FCSTD DOCUMENT  (FreeCAD 0.20R)
Label: even_better_inner_plate
License: All rights reserved
LicenseURL: http://en.wikipedia.org/wiki/All_rights_reserved
objects: Sketcher::SketchObject×1
note: 1 computed .brp shape members not serialized (recipe doc carries the construction recipe); baked Part::Feature solids carry a one-line shape summary decoded from their .brp

FEATURE [Sketcher::SketchObject] Sketch
  FullyConstrained = true
  sketch-geometry (934):
    g0: LineSegment StartX=3.025 StartY=-7.2875 StartZ=0 EndX=16.025 EndY=-7.2875 EndZ=0
    g1: LineSegment StartX=3.025 StartY=-21.2875 StartZ=0 EndX=16.025 EndY=-21.2875 EndZ=0
    g2: LineSegment StartX=2.525 StartY=-7.7875 StartZ=0 EndX=2.525 EndY=-20.7875 EndZ=0
    g3: LineSegment StartX=16.525 StartY=-7.7875 StartZ=0 EndX=16.525 EndY=-20.7875 EndZ=0
    g4: ArcOfCircle CenterX=3.025 CenterY=-7.7875 CenterZ=0 NormalX=0 NormalY=0 NormalZ=1 AngleXU=0 Radius=0.5 StartAngle=1.5708 EndAngle=3.14159
    g5: ArcOfCircle CenterX=16.025 CenterY=-7.7875 CenterZ=0 NormalX=0 NormalY=0 NormalZ=1 AngleXU=0 Radius=0.5 StartAngle=0 EndAngle=1.5708
    g6: ArcOfCircle CenterX=3.025 CenterY=-20.7875 CenterZ=0 NormalX=0 NormalY=0 NormalZ=1 AngleXU=0 Radius=0.5 StartAngle=3.14159 EndAngle=4.71239
    g7: ArcOfCircle CenterX=16.025 CenterY=-20.7875 CenterZ=0 NormalX=0 NormalY=0 NormalZ=1 AngleXU=0 Radius=0.5 StartAngle=4.71239 EndAngle=6.28319
    g8: LineSegment StartX=41.125 StartY=-7.2875 StartZ=0 EndX=54.125 EndY=-7.2875 EndZ=0
    g9: LineSegment StartX=41.125 StartY=-21.2875 StartZ=0 EndX=54.125 EndY=-21.2875 EndZ=0
    g10: LineSegment StartX=40.625 StartY=-7.7875 StartZ=0 EndX=40.625 EndY=-20.7875 EndZ=0
    g11: LineSegment StartX=54.625 StartY=-7.7875 StartZ=0 EndX=54.625 EndY=-20.7875 EndZ=0
    g12: ArcOfCircle CenterX=41.125 CenterY=-7.7875 CenterZ=0 NormalX=0 NormalY=0 NormalZ=1 AngleXU=0 Radius=0.5 StartAngle=1.5708 EndAngle=3.14159
    g13: ArcOfCircle CenterX=54.125 CenterY=-7.7875 CenterZ=0 NormalX=0 NormalY=0 NormalZ=1 AngleXU=0 Radius=0.5 StartAngle=0 EndAngle=1.5708
    g14: ArcOfCircle CenterX=41.125 CenterY=-20.7875 CenterZ=0 NormalX=0 NormalY=0 NormalZ=1 AngleXU=0 Radius=0.5 StartAngle=3.14159 EndAngle=4.71239
    g15: ArcOfCircle CenterX=54.125 CenterY=-20.7875 CenterZ=0 NormalX=0 NormalY=0 NormalZ=1 AngleXU=0 Radius=0.5 StartAngle=4.71239 EndAngle=6.28319
    g16: LineSegment StartX=60.175 StartY=-7.2875 StartZ=0 EndX=73.175 EndY=-7.2875 EndZ=0
    g17: LineSegment StartX=60.175 StartY=-21.2875 StartZ=0 EndX=73.175 EndY=-21.2875 EndZ=0
    g18: LineSegment StartX=59.675 StartY=-7.7875 StartZ=0 EndX=59.675 EndY=-20.7875 EndZ=0
    g19: LineSegment StartX=73.675 StartY=-7.7875 StartZ=0 EndX=73.675 EndY=-20.7875 EndZ=0
    g20: ArcOfCircle CenterX=60.175 CenterY=-7.7875 CenterZ=0 NormalX=0 NormalY=0 NormalZ=1 AngleXU=0 Radius=0.5 StartAngle=1.5708 EndAngle=3.14159
    g21: ArcOfCircle CenterX=73.175 CenterY=-7.7875 CenterZ=0 NormalX=0 NormalY=0 NormalZ=1 AngleXU=0 Radius=0.5 StartAngle=0 EndAngle=1.5708
    g22: ArcOfCircle CenterX=60.175 CenterY=-20.7875 CenterZ=0 NormalX=0 NormalY=0 NormalZ=1 AngleXU=0 Radius=0.5 StartAngle=3.14159 EndAngle=4.71239
    g23: ArcOfCircle CenterX=73.175 CenterY=-20.7875 CenterZ=0 NormalX=0 NormalY=0 NormalZ=1 AngleXU=0 Radius=0.5 StartAngle=4.71239 EndAngle=6.28319
    g24: LineSegment StartX=79.225 StartY=-7.2875 StartZ=0 EndX=92.225 EndY=-7.2875 EndZ=0
    g25: LineSegment StartX=79.225 StartY=-21.2875 StartZ=0 EndX=92.225 EndY=-21.2875 EndZ=0
    g26: LineSegment StartX=78.725 StartY=-7.7875 StartZ=0 EndX=78.725 EndY=-20.7875 EndZ=0
    g27: LineSegment StartX=92.725 StartY=-7.7875 StartZ=0 EndX=92.725 EndY=-20.7875 EndZ=0
    g28: ArcOfCircle CenterX=79.225 CenterY=-7.7875 CenterZ=0 NormalX=0 NormalY=0 NormalZ=1 AngleXU=0 Radius=0.5 StartAngle=1.5708 EndAngle=3.14159
    g29: ArcOfCircle CenterX=92.225 CenterY=-7.7875 CenterZ=0 NormalX=0 NormalY=0 NormalZ=1 AngleXU=0 Radius=0.5 StartAngle=0 EndAngle=1.5708
    g30: ArcOfCircle CenterX=79.225 CenterY=-20.7875 CenterZ=0 NormalX=0 NormalY=0 NormalZ=1 AngleXU=0 Radius=0.5 StartAngle=3.14159 EndAngle=4.71239
    g31: ArcOfCircle CenterX=92.225 CenterY=-20.7875 CenterZ=0 NormalX=0 NormalY=0 NormalZ=1 AngleXU=0 Radius=0.5 StartAngle=4.71239 EndAngle=6.28319
    g32: LineSegment StartX=98.275 StartY=-7.2875 StartZ=0 EndX=111.275 EndY=-7.2875 EndZ=0
    g33: LineSegment StartX=98.275 StartY=-21.2875 StartZ=0 EndX=111.275 EndY=-21.2875 EndZ=0
    g34: LineSegment StartX=97.775 StartY=-7.7875 StartZ=0 EndX=97.775 EndY=-20.7875 EndZ=0
    g35: LineSegment StartX=111.775 StartY=-7.7875 StartZ=0 EndX=111.775 EndY=-20.7875 EndZ=0
    g36: ArcOfCircle CenterX=98.275 CenterY=-7.7875 CenterZ=0 NormalX=0 NormalY=0 NormalZ=1 AngleXU=0 Radius=0.5 StartAngle=1.5708 EndAngle=3.14159
    g37: ArcOfCircle CenterX=111.275 CenterY=-7.7875 CenterZ=0 NormalX=0 NormalY=0 NormalZ=1 AngleXU=0 Radius=0.5 StartAngle=0 EndAngle=1.5708
    g38: ArcOfCircle CenterX=98.275 CenterY=-20.7875 CenterZ=0 NormalX=0 NormalY=0 NormalZ=1 AngleXU=0 Radius=0.5 StartAngle=3.14159 EndAngle=4.71239
    g39: ArcOfCircle CenterX=111.275 CenterY=-20.7875 CenterZ=0 NormalX=0 NormalY=0 NormalZ=1 AngleXU=0 Radius=0.5 StartAngle=4.71239 EndAngle=6.28319
    g40: LineSegment StartX=126.85 StartY=-7.2875 StartZ=0 EndX=139.85 EndY=-7.2875 EndZ=0
    g41: LineSegment StartX=126.85 StartY=-21.2875 StartZ=0 EndX=139.85 EndY=-21.2875 EndZ=0
    g42: LineSegment StartX=126.35 StartY=-7.7875 StartZ=0 EndX=126.35 EndY=-20.7875 EndZ=0
    g43: LineSegment StartX=140.35 StartY=-7.7875 StartZ=0 EndX=140.35 EndY=-20.7875 EndZ=0
    g44: ArcOfCircle CenterX=126.85 CenterY=-7.7875 CenterZ=0 NormalX=0 NormalY=0 NormalZ=1 AngleXU=0 Radius=0.5 StartAngle=1.5708 EndAngle=3.14159
    g45: ArcOfCircle CenterX=139.85 CenterY=-7.7875 CenterZ=0 NormalX=0 NormalY=0 NormalZ=1 AngleXU=0 Radius=0.5 StartAngle=0 EndAngle=1.5708
    g46: ArcOfCircle CenterX=126.85 CenterY=-20.7875 CenterZ=0 NormalX=0 NormalY=0 NormalZ=1 AngleXU=0 Radius=0.5 StartAngle=3.14159 EndAngle=4.71239
    g47: ArcOfCircle CenterX=139.85 CenterY=-20.7875 CenterZ=0 NormalX=0 NormalY=0 NormalZ=1 AngleXU=0 Radius=0.5 StartAngle=4.71239 EndAngle=6.28319
    g48: LineSegment StartX=145.9 StartY=-7.2875 StartZ=0 EndX=158.9 EndY=-7.2875 EndZ=0
    g49: LineSegment StartX=145.9 StartY=-21.2875 StartZ=0 EndX=158.9 EndY=-21.2875 EndZ=0
    g50: LineSegment StartX=145.4 StartY=-7.7875 StartZ=0 EndX=145.4 EndY=-20.7875 EndZ=0
    g51: LineSegment StartX=159.4 StartY=-7.7875 StartZ=0 EndX=159.4 EndY=-20.7875 EndZ=0
    g52: ArcOfCircle CenterX=145.9 CenterY=-7.7875 CenterZ=0 NormalX=0 NormalY=0 NormalZ=1 AngleXU=0 Radius=0.5 StartAngle=1.5708 EndAngle=3.14159
    g53: ArcOfCircle CenterX=158.9 CenterY=-7.7875 CenterZ=0 NormalX=0 NormalY=0 NormalZ=1 AngleXU=0 Radius=0.5 StartAngle=0 EndAngle=1.5708
    g54: ArcOfCircle CenterX=145.9 CenterY=-20.7875 CenterZ=0 NormalX=0 NormalY=0 NormalZ=1 AngleXU=0 Radius=0.5 StartAngle=3.14159 EndAngle=4.71239
    g55: ArcOfCircle CenterX=158.9 CenterY=-20.7875 CenterZ=0 NormalX=0 NormalY=0 NormalZ=1 AngleXU=0 Radius=0.5 StartAngle=4.71239 EndAngle=6.28319
    g56: LineSegment StartX=164.95 StartY=-7.2875 StartZ=0 EndX=177.95 EndY=-7.2875 EndZ=0
    g57: LineSegment StartX=164.95 StartY=-21.2875 StartZ=0 EndX=177.95 EndY=-21.2875 EndZ=0
    g58: LineSegment StartX=164.45 StartY=-7.7875 StartZ=0 EndX=164.45 EndY=-20.7875 EndZ=0
    g59: LineSegment StartX=178.45 StartY=-7.7875 StartZ=0 EndX=178.45 EndY=-20.7875 EndZ=0
    g60: ArcOfCircle CenterX=164.95 CenterY=-7.7875 CenterZ=0 NormalX=0 NormalY=0 NormalZ=1 AngleXU=0 Radius=0.5 StartAngle=1.5708 EndAngle=3.14159
    g61: ArcOfCircle CenterX=177.95 CenterY=-7.7875 CenterZ=0 NormalX=0 NormalY=0 NormalZ=1 AngleXU=0 Radius=0.5 StartAngle=0 EndAngle=1.5708
    g62: ArcOfCircle CenterX=164.95 CenterY=-20.7875 CenterZ=0 NormalX=0 NormalY=0 NormalZ=1 AngleXU=0 Radius=0.5 StartAngle=3.14159 EndAngle=4.71239
    g63: ArcOfCircle CenterX=177.95 CenterY=-20.7875 CenterZ=0 NormalX=0 NormalY=0 NormalZ=1 AngleXU=0 Radius=0.5 StartAngle=4.71239 EndAngle=6.28319
    g64: LineSegment StartX=184 StartY=-7.2875 StartZ=0 EndX=197 EndY=-7.2875 EndZ=0
    g65: LineSegment StartX=184 StartY=-21.2875 StartZ=0 EndX=197 EndY=-21.2875 EndZ=0
    g66: LineSegment StartX=183.5 StartY=-7.7875 StartZ=0 EndX=183.5 EndY=-20.7875 EndZ=0
    g67: LineSegment StartX=197.5 StartY=-7.7875 StartZ=0 EndX=197.5 EndY=-20.7875 EndZ=0
    g68: ArcOfCircle CenterX=184 CenterY=-7.7875 CenterZ=0 NormalX=0 NormalY=0 NormalZ=1 AngleXU=0 Radius=0.5 StartAngle=1.5708 EndAngle=3.14159
    g69: ArcOfCircle CenterX=197 CenterY=-7.7875 CenterZ=0 NormalX=0 NormalY=0 NormalZ=1 AngleXU=0 Radius=0.5 StartAngle=0 EndAngle=1.5708
    g70: ArcOfCircle CenterX=184 CenterY=-20.7875 CenterZ=0 NormalX=0 NormalY=0 NormalZ=1 AngleXU=0 Radius=0.5 StartAngle=3.14159 EndAngle=4.71239
    g71: ArcOfCircle CenterX=197 CenterY=-20.7875 CenterZ=0 NormalX=0 NormalY=0 NormalZ=1 AngleXU=0 Radius=0.5 StartAngle=4.71239 EndAngle=6.28319
    g72: LineSegment StartX=212.575 StartY=-7.2875 StartZ=0 EndX=225.575 EndY=-7.2875 EndZ=0
    g73: LineSegment StartX=212.575 StartY=-21.2875 StartZ=0 EndX=225.575 EndY=-21.2875 EndZ=0
    g74: LineSegment StartX=212.075 StartY=-7.7875 StartZ=0 EndX=212.075 EndY=-20.7875 EndZ=0
    g75: LineSegment StartX=226.075 StartY=-7.7875 StartZ=0 EndX=226.075 EndY=-20.7875 EndZ=0
    g76: ArcOfCircle CenterX=212.575 CenterY=-7.7875 CenterZ=0 NormalX=0 NormalY=0 NormalZ=1 AngleXU=0 Radius=0.5 StartAngle=1.5708 EndAngle=3.14159
    g77: ArcOfCircle CenterX=225.575 CenterY=-7.7875 CenterZ=0 NormalX=0 NormalY=0 NormalZ=1 AngleXU=0 Radius=0.5 StartAngle=0 EndAngle=1.5708
    g78: ArcOfCircle CenterX=212.575 CenterY=-20.7875 CenterZ=0 NormalX=0 NormalY=0 NormalZ=1 AngleXU=0 Radius=0.5 StartAngle=3.14159 EndAngle=4.71239
    g79: ArcOfCircle CenterX=225.575 CenterY=-20.7875 CenterZ=0 NormalX=0 NormalY=0 NormalZ=1 AngleXU=0 Radius=0.5 StartAngle=4.71239 EndAngle=6.28319
    g80: LineSegment StartX=231.625 StartY=-7.2875 StartZ=0 EndX=244.625 EndY=-7.2875 EndZ=0
    g81: LineSegment StartX=231.625 StartY=-21.2875 StartZ=0 EndX=244.625 EndY=-21.2875 EndZ=0
    g82: LineSegment StartX=231.125 StartY=-7.7875 StartZ=0 EndX=231.125 EndY=-20.7875 EndZ=0
    g83: LineSegment StartX=245.125 StartY=-7.7875 StartZ=0 EndX=245.125 EndY=-20.7875 EndZ=0
    g84: ArcOfCircle CenterX=231.625 CenterY=-7.7875 CenterZ=0 NormalX=0 NormalY=0 NormalZ=1 AngleXU=0 Radius=0.5 StartAngle=1.5708 EndAngle=3.14159
    g85: ArcOfCircle CenterX=244.625 CenterY=-7.7875 CenterZ=0 NormalX=0 NormalY=0 NormalZ=1 AngleXU=0 Radius=0.5 StartAngle=0 EndAngle=1.5708
    g86: ArcOfCircle CenterX=231.625 CenterY=-20.7875 CenterZ=0 NormalX=0 NormalY=0 NormalZ=1 AngleXU=0 Radius=0.5 StartAngle=3.14159 EndAngle=4.71239
    g87: ArcOfCircle CenterX=244.625 CenterY=-20.7875 CenterZ=0 NormalX=0 NormalY=0 NormalZ=1 AngleXU=0 Radius=0.5 StartAngle=4.71239 EndAngle=6.28319
    g88: LineSegment StartX=250.675 StartY=-7.2875 StartZ=0 EndX=263.675 EndY=-7.2875 EndZ=0
    g89: LineSegment StartX=250.675 StartY=-21.2875 StartZ=0 EndX=263.675 EndY=-21.2875 EndZ=0
    g90: LineSegment StartX=250.175 StartY=-7.7875 StartZ=0 EndX=250.175 EndY=-20.7875 EndZ=0
    g91: LineSegment StartX=264.175 StartY=-7.7875 StartZ=0 EndX=264.175 EndY=-20.7875 EndZ=0
    g92: ArcOfCircle CenterX=250.675 CenterY=-7.7875 CenterZ=0 NormalX=0 NormalY=0 NormalZ=1 AngleXU=0 Radius=0.5 StartAngle=1.5708 EndAngle=3.14159
    g93: ArcOfCircle CenterX=263.675 CenterY=-7.7875 CenterZ=0 NormalX=0 NormalY=0 NormalZ=1 AngleXU=0 Radius=0.5 StartAngle=0 EndAngle=1.5708
    g94: ArcOfCircle CenterX=250.675 CenterY=-20.7875 CenterZ=0 NormalX=0 NormalY=0 NormalZ=1 AngleXU=0 Radius=0.5 StartAngle=3.14159 EndAngle=4.71239
    g95: ArcOfCircle CenterX=263.675 CenterY=-20.7875 CenterZ=0 NormalX=0 NormalY=0 NormalZ=1 AngleXU=0 Radius=0.5 StartAngle=4.71239 EndAngle=6.28319
    g96: LineSegment StartX=269.725 StartY=-7.2875 StartZ=0 EndX=282.725 EndY=-7.2875 EndZ=0
    g97: LineSegment StartX=269.725 StartY=-21.2875 StartZ=0 EndX=282.725 EndY=-21.2875 EndZ=0
    g98: LineSegment StartX=269.225 StartY=-7.7875 StartZ=0 EndX=269.225 EndY=-20.7875 EndZ=0
    g99: LineSegment StartX=283.225 StartY=-7.7875 StartZ=0 EndX=283.225 EndY=-20.7875 EndZ=0
    g100: ArcOfCircle CenterX=269.725 CenterY=-7.7875 CenterZ=0 NormalX=0 NormalY=0 NormalZ=1 AngleXU=0 Radius=0.5 StartAngle=1.5708 EndAngle=3.14159
    g101: ArcOfCircle CenterX=282.725 CenterY=-7.7875 CenterZ=0 NormalX=0 NormalY=0 NormalZ=1 AngleXU=0 Radius=0.5 StartAngle=0 EndAngle=1.5708
    g102: ArcOfCircle CenterX=269.725 CenterY=-20.7875 CenterZ=0 NormalX=0 NormalY=0 NormalZ=1 AngleXU=0 Radius=0.5 StartAngle=3.14159 EndAngle=4.71239
    g103: ArcOfCircle CenterX=282.725 CenterY=-20.7875 CenterZ=0 NormalX=0 NormalY=0 NormalZ=1 AngleXU=0 Radius=0.5 StartAngle=4.71239 EndAngle=6.28319
    g104: LineSegment StartX=3.025 StartY=-31.1 StartZ=0 EndX=16.025 EndY=-31.1 EndZ=0
    g105: LineSegment StartX=3.025 StartY=-45.1 StartZ=0 EndX=16.025 EndY=-45.1 EndZ=0
    g106: LineSegment StartX=2.525 StartY=-31.6 StartZ=0 EndX=2.525 EndY=-44.6 EndZ=0
    g107: LineSegment StartX=16.525 StartY=-31.6 StartZ=0 EndX=16.525 EndY=-44.6 EndZ=0
    g108: ArcOfCircle CenterX=3.025 CenterY=-31.6 CenterZ=0 NormalX=0 NormalY=0 NormalZ=1 AngleXU=0 Radius=0.5 StartAngle=1.5708 EndAngle=3.14159
    g109: ArcOfCircle CenterX=16.025 CenterY=-31.6 CenterZ=0 NormalX=0 NormalY=0 NormalZ=1 AngleXU=0 Radius=0.5 StartAngle=0 EndAngle=1.5708
    g110: ArcOfCircle CenterX=3.025 CenterY=-44.6 CenterZ=0 NormalX=0 NormalY=0 NormalZ=1 AngleXU=0 Radius=0.5 StartAngle=3.14159 EndAngle=4.71239
    g111: ArcOfCircle CenterX=16.025 CenterY=-44.6 CenterZ=0 NormalX=0 NormalY=0 NormalZ=1 AngleXU=0 Radius=0.5 StartAngle=4.71239 EndAngle=6.28319
    g112: LineSegment StartX=22.075 StartY=-31.1 StartZ=0 EndX=35.075 EndY=-31.1 EndZ=0
    g113: LineSegment StartX=22.075 StartY=-45.1 StartZ=0 EndX=35.075 EndY=-45.1 EndZ=0
    g114: LineSegment StartX=21.575 StartY=-31.6 StartZ=0 EndX=21.575 EndY=-44.6 EndZ=0
    g115: LineSegment StartX=35.575 StartY=-31.6 StartZ=0 EndX=35.575 EndY=-44.6 EndZ=0
    g116: ArcOfCircle CenterX=22.075 CenterY=-31.6 CenterZ=0 NormalX=0 NormalY=0 NormalZ=1 AngleXU=0 Radius=0.5 StartAngle=1.5708 EndAngle=3.14159
    g117: ArcOfCircle CenterX=35.075 CenterY=-31.6 CenterZ=0 NormalX=0 NormalY=0 NormalZ=1 AngleXU=0 Radius=0.5 StartAngle=0 EndAngle=1.5708
    g118: ArcOfCircle CenterX=22.075 CenterY=-44.6 CenterZ=0 NormalX=0 NormalY=0 NormalZ=1 AngleXU=0 Radius=0.5 StartAngle=3.14159 EndAngle=4.71239
    g119: ArcOfCircle CenterX=35.075 CenterY=-44.6 CenterZ=0 NormalX=0 NormalY=0 NormalZ=1 AngleXU=0 Radius=0.5 StartAngle=4.71239 EndAngle=6.28319
    g120: LineSegment StartX=41.125 StartY=-31.1 StartZ=0 EndX=54.125 EndY=-31.1 EndZ=0
    g121: LineSegment StartX=41.125 StartY=-45.1 StartZ=0 EndX=54.125 EndY=-45.1 EndZ=0
    g122: LineSegment StartX=40.625 StartY=-31.6 StartZ=0 EndX=40.625 EndY=-44.6 EndZ=0
    g123: LineSegment StartX=54.625 StartY=-31.6 StartZ=0 EndX=54.625 EndY=-44.6 EndZ=0
    g124: ArcOfCircle CenterX=41.125 CenterY=-31.6 CenterZ=0 NormalX=0 NormalY=0 NormalZ=1 AngleXU=0 Radius=0.5 StartAngle=1.5708 EndAngle=3.14159
    g125: ArcOfCircle CenterX=54.125 CenterY=-31.6 CenterZ=0 NormalX=0 NormalY=0 NormalZ=1 AngleXU=0 Radius=0.5 StartAngle=0 EndAngle=1.5708
    g126: ArcOfCircle CenterX=41.125 CenterY=-44.6 CenterZ=0 NormalX=0 NormalY=0 NormalZ=1 AngleXU=0 Radius=0.5 StartAngle=3.14159 EndAngle=4.71239
    g127: ArcOfCircle CenterX=54.125 CenterY=-44.6 CenterZ=0 NormalX=0 NormalY=0 NormalZ=1 AngleXU=0 Radius=0.5 StartAngle=4.71239 EndAngle=6.28319
    g128: LineSegment StartX=60.175 StartY=-31.1 StartZ=0 EndX=73.175 EndY=-31.1 EndZ=0
    g129: LineSegment StartX=60.175 StartY=-45.1 StartZ=0 EndX=73.175 EndY=-45.1 EndZ=0
    g130: LineSegment StartX=59.675 StartY=-31.6 StartZ=0 EndX=59.675 EndY=-44.6 EndZ=0
    g131: LineSegment StartX=73.675 StartY=-31.6 StartZ=0 EndX=73.675 EndY=-44.6 EndZ=0
    g132: ArcOfCircle CenterX=60.175 CenterY=-31.6 CenterZ=0 NormalX=0 NormalY=0 NormalZ=1 AngleXU=0 Radius=0.5 StartAngle=1.5708 EndAngle=3.14159
    g133: ArcOfCircle CenterX=73.175 CenterY=-31.6 CenterZ=0 NormalX=0 NormalY=0 NormalZ=1 AngleXU=0 Radius=0.5 StartAngle=0 EndAngle=1.5708
    g134: ArcOfCircle CenterX=60.175 CenterY=-44.6 CenterZ=0 NormalX=0 NormalY=0 NormalZ=1 AngleXU=0 Radius=0.5 StartAngle=3.14159 EndAngle=4.71239
    g135: ArcOfCircle CenterX=73.175 CenterY=-44.6 CenterZ=0 NormalX=0 NormalY=0 NormalZ=1 AngleXU=0 Radius=0.5 StartAngle=4.71239 EndAngle=6.28319
    g136: LineSegment StartX=79.225 StartY=-31.1 StartZ=0 EndX=92.225 EndY=-31.1 EndZ=0
    g137: LineSegment StartX=79.225 StartY=-45.1 StartZ=0 EndX=92.225 EndY=-45.1 EndZ=0
    g138: LineSegment StartX=78.725 StartY=-31.6 StartZ=0 EndX=78.725 EndY=-44.6 EndZ=0
    g139: LineSegment StartX=92.725 StartY=-31.6 StartZ=0 EndX=92.725 EndY=-44.6 EndZ=0
    g140: ArcOfCircle CenterX=79.225 CenterY=-31.6 CenterZ=0 NormalX=0 NormalY=0 NormalZ=1 AngleXU=0 Radius=0.5 StartAngle=1.5708 EndAngle=3.14159
    g141: ArcOfCircle CenterX=92.225 CenterY=-31.6 CenterZ=0 NormalX=0 NormalY=0 NormalZ=1 AngleXU=0 Radius=0.5 StartAngle=0 EndAngle=1.5708
    g142: ArcOfCircle CenterX=79.225 CenterY=-44.6 CenterZ=0 NormalX=0 NormalY=0 NormalZ=1 AngleXU=0 Radius=0.5 StartAngle=3.14159 EndAngle=4.71239
    g143: ArcOfCircle CenterX=92.225 CenterY=-44.6 CenterZ=0 NormalX=0 NormalY=0 NormalZ=1 AngleXU=0 Radius=0.5 StartAngle=4.71239 EndAngle=6.28319
    g144: LineSegment StartX=98.275 StartY=-31.1 StartZ=0 EndX=111.275 EndY=-31.1 EndZ=0
    g145: LineSegment StartX=98.275 StartY=-45.1 StartZ=0 EndX=111.275 EndY=-45.1 EndZ=0
    g146: LineSegment StartX=97.775 StartY=-31.6 StartZ=0 EndX=97.775 EndY=-44.6 EndZ=0
    g147: LineSegment StartX=111.775 StartY=-31.6 StartZ=0 EndX=111.775 EndY=-44.6 EndZ=0
    g148: ArcOfCircle CenterX=98.275 CenterY=-31.6 CenterZ=0 NormalX=0 NormalY=0 NormalZ=1 AngleXU=0 Radius=0.5 StartAngle=1.5708 EndAngle=3.14159
    g149: ArcOfCircle CenterX=111.275 CenterY=-31.6 CenterZ=0 NormalX=0 NormalY=0 NormalZ=1 AngleXU=0 Radius=0.5 StartAngle=0 EndAngle=1.5708
    g150: ArcOfCircle CenterX=98.275 CenterY=-44.6 CenterZ=0 NormalX=0 NormalY=0 NormalZ=1 AngleXU=0 Radius=0.5 StartAngle=3.14159 EndAngle=4.71239
    g151: ArcOfCircle CenterX=111.275 CenterY=-44.6 CenterZ=0 NormalX=0 NormalY=0 NormalZ=1 AngleXU=0 Radius=0.5 StartAngle=4.71239 EndAngle=6.28319
    g152: LineSegment StartX=117.325 StartY=-31.1 StartZ=0 EndX=130.325 EndY=-31.1 EndZ=0
    g153: LineSegment StartX=117.325 StartY=-45.1 StartZ=0 EndX=130.325 EndY=-45.1 EndZ=0
    g154: LineSegment StartX=116.825 StartY=-31.6 StartZ=0 EndX=116.825 EndY=-44.6 EndZ=0
    g155: LineSegment StartX=130.825 StartY=-31.6 StartZ=0 EndX=130.825 EndY=-44.6 EndZ=0
    g156: ArcOfCircle CenterX=117.325 CenterY=-31.6 CenterZ=0 NormalX=0 NormalY=0 NormalZ=1 AngleXU=0 Radius=0.5 StartAngle=1.5708 EndAngle=3.14159
    g157: ArcOfCircle CenterX=130.325 CenterY=-31.6 CenterZ=0 NormalX=0 NormalY=0 NormalZ=1 AngleXU=0 Radius=0.5 StartAngle=0 EndAngle=1.5708
    g158: ArcOfCircle CenterX=117.325 CenterY=-44.6 CenterZ=0 NormalX=0 NormalY=0 NormalZ=1 AngleXU=0 Radius=0.5 StartAngle=3.14159 EndAngle=4.71239
    g159: ArcOfCircle CenterX=130.325 CenterY=-44.6 CenterZ=0 NormalX=0 NormalY=0 NormalZ=1 AngleXU=0 Radius=0.5 StartAngle=4.71239 EndAngle=6.28319
    g160: LineSegment StartX=136.375 StartY=-31.1 StartZ=0 EndX=149.375 EndY=-31.1 EndZ=0
    g161: LineSegment StartX=136.375 StartY=-45.1 StartZ=0 EndX=149.375 EndY=-45.1 EndZ=0
    g162: LineSegment StartX=135.875 StartY=-31.6 StartZ=0 EndX=135.875 EndY=-44.6 EndZ=0
    g163: LineSegment StartX=149.875 StartY=-31.6 StartZ=0 EndX=149.875 EndY=-44.6 EndZ=0
    g164: ArcOfCircle CenterX=136.375 CenterY=-31.6 CenterZ=0 NormalX=0 NormalY=0 NormalZ=1 AngleXU=0 Radius=0.5 StartAngle=1.5708 EndAngle=3.14159
    g165: ArcOfCircle CenterX=149.375 CenterY=-31.6 CenterZ=0 NormalX=0 NormalY=0 NormalZ=1 AngleXU=0 Radius=0.5 StartAngle=0 EndAngle=1.5708
    g166: ArcOfCircle CenterX=136.375 CenterY=-44.6 CenterZ=0 NormalX=0 NormalY=0 NormalZ=1 AngleXU=0 Radius=0.5 StartAngle=3.14159 EndAngle=4.71239
    g167: ArcOfCircle CenterX=149.375 CenterY=-44.6 CenterZ=0 NormalX=0 NormalY=0 NormalZ=1 AngleXU=0 Radius=0.5 StartAngle=4.71239 EndAngle=6.28319
    g168: LineSegment StartX=155.425 StartY=-31.1 StartZ=0 EndX=168.425 EndY=-31.1 EndZ=0
    g169: LineSegment StartX=155.425 StartY=-45.1 StartZ=0 EndX=168.425 EndY=-45.1 EndZ=0
    g170: LineSegment StartX=154.925 StartY=-31.6 StartZ=0 EndX=154.925 EndY=-44.6 EndZ=0
    g171: LineSegment StartX=168.925 StartY=-31.6 StartZ=0 EndX=168.925 EndY=-44.6 EndZ=0
    g172: ArcOfCircle CenterX=155.425 CenterY=-31.6 CenterZ=0 NormalX=0 NormalY=0 NormalZ=1 AngleXU=0 Radius=0.5 StartAngle=1.5708 EndAngle=3.14159
    g173: ArcOfCircle CenterX=168.425 CenterY=-31.6 CenterZ=0 NormalX=0 NormalY=0 NormalZ=1 AngleXU=0 Radius=0.5 StartAngle=0 EndAngle=1.5708
    g174: ArcOfCircle CenterX=155.425 CenterY=-44.6 CenterZ=0 NormalX=0 NormalY=0 NormalZ=1 AngleXU=0 Radius=0.5 StartAngle=3.14159 EndAngle=4.71239
    g175: ArcOfCircle CenterX=168.425 CenterY=-44.6 CenterZ=0 NormalX=0 NormalY=0 NormalZ=1 AngleXU=0 Radius=0.5 StartAngle=4.71239 EndAngle=6.28319
    g176: LineSegment StartX=174.475 StartY=-31.1 StartZ=0 EndX=187.475 EndY=-31.1 EndZ=0
    g177: LineSegment StartX=174.475 StartY=-45.1 StartZ=0 EndX=187.475 EndY=-45.1 EndZ=0
    g178: LineSegment StartX=173.975 StartY=-31.6 StartZ=0 EndX=173.975 EndY=-44.6 EndZ=0
    g179: LineSegment StartX=187.975 StartY=-31.6 StartZ=0 EndX=187.975 EndY=-44.6 EndZ=0
    g180: ArcOfCircle CenterX=174.475 CenterY=-31.6 CenterZ=0 NormalX=0 NormalY=0 NormalZ=1 AngleXU=0 Radius=0.5 StartAngle=1.5708 EndAngle=3.14159
    g181: ArcOfCircle CenterX=187.475 CenterY=-31.6 CenterZ=0 NormalX=0 NormalY=0 NormalZ=1 AngleXU=0 Radius=0.5 StartAngle=0 EndAngle=1.5708
    g182: ArcOfCircle CenterX=174.475 CenterY=-44.6 CenterZ=0 NormalX=0 NormalY=0 NormalZ=1 AngleXU=0 Radius=0.5 StartAngle=3.14159 EndAngle=4.71239
    g183: ArcOfCircle CenterX=187.475 CenterY=-44.6 CenterZ=0 NormalX=0 NormalY=0 NormalZ=1 AngleXU=0 Radius=0.5 StartAngle=4.71239 EndAngle=6.28319
    g184: LineSegment StartX=193.525 StartY=-31.1 StartZ=0 EndX=206.525 EndY=-31.1 EndZ=0
    g185: LineSegment StartX=193.525 StartY=-45.1 StartZ=0 EndX=206.525 EndY=-45.1 EndZ=0
    g186: LineSegment StartX=193.025 StartY=-31.6 StartZ=0 EndX=193.025 EndY=-44.6 EndZ=0
    g187: LineSegment StartX=207.025 StartY=-31.6 StartZ=0 EndX=207.025 EndY=-44.6 EndZ=0
    g188: ArcOfCircle CenterX=193.525 CenterY=-31.6 CenterZ=0 NormalX=0 NormalY=0 NormalZ=1 AngleXU=0 Radius=0.5 StartAngle=1.5708 EndAngle=3.14159
    g189: ArcOfCircle CenterX=206.525 CenterY=-31.6 CenterZ=0 NormalX=0 NormalY=0 NormalZ=1 AngleXU=0 Radius=0.5 StartAngle=0 EndAngle=1.5708
    g190: ArcOfCircle CenterX=193.525 CenterY=-44.6 CenterZ=0 NormalX=0 NormalY=0 NormalZ=1 AngleXU=0 Radius=0.5 StartAngle=3.14159 EndAngle=4.71239
    g191: ArcOfCircle CenterX=206.525 CenterY=-44.6 CenterZ=0 NormalX=0 NormalY=0 NormalZ=1 AngleXU=0 Radius=0.5 StartAngle=4.71239 EndAngle=6.28319
    g192: LineSegment StartX=212.575 StartY=-31.1 StartZ=0 EndX=225.575 EndY=-31.1 EndZ=0
    g193: LineSegment StartX=212.575 StartY=-45.1 StartZ=0 EndX=225.575 EndY=-45.1 EndZ=0
    g194: LineSegment StartX=212.075 StartY=-31.6 StartZ=0 EndX=212.075 EndY=-44.6 EndZ=0
    g195: LineSegment StartX=226.075 StartY=-31.6 StartZ=0 EndX=226.075 EndY=-44.6 EndZ=0
    g196: ArcOfCircle CenterX=212.575 CenterY=-31.6 CenterZ=0 NormalX=0 NormalY=0 NormalZ=1 AngleXU=0 Radius=0.5 StartAngle=1.5708 EndAngle=3.14159
    g197: ArcOfCircle CenterX=225.575 CenterY=-31.6 CenterZ=0 NormalX=0 NormalY=0 NormalZ=1 AngleXU=0 Radius=0.5 StartAngle=0 EndAngle=1.5708
    g198: ArcOfCircle CenterX=212.575 CenterY=-44.6 CenterZ=0 NormalX=0 NormalY=0 NormalZ=1 AngleXU=0 Radius=0.5 StartAngle=3.14159 EndAngle=4.71239
    g199: ArcOfCircle CenterX=225.575 CenterY=-44.6 CenterZ=0 NormalX=0 NormalY=0 NormalZ=1 AngleXU=0 Radius=0.5 StartAngle=4.71239 EndAngle=6.28319
    g200: LineSegment StartX=231.625 StartY=-31.1 StartZ=0 EndX=244.625 EndY=-31.1 EndZ=0
    g201: LineSegment StartX=231.625 StartY=-45.1 StartZ=0 EndX=244.625 EndY=-45.1 EndZ=0
    g202: LineSegment StartX=231.125 StartY=-31.6 StartZ=0 EndX=231.125 EndY=-44.6 EndZ=0
    g203: LineSegment StartX=245.125 StartY=-31.6 StartZ=0 EndX=245.125 EndY=-44.6 EndZ=0
    g204: ArcOfCircle CenterX=231.625 CenterY=-31.6 CenterZ=0 NormalX=0 NormalY=0 NormalZ=1 AngleXU=0 Radius=0.5 StartAngle=1.5708 EndAngle=3.14159
    g205: ArcOfCircle CenterX=244.625 CenterY=-31.6 CenterZ=0 NormalX=0 NormalY=0 NormalZ=1 AngleXU=0 Radius=0.5 StartAngle=0 EndAngle=1.5708
    g206: ArcOfCircle CenterX=231.625 CenterY=-44.6 CenterZ=0 NormalX=0 NormalY=0 NormalZ=1 AngleXU=0 Radius=0.5 StartAngle=3.14159 EndAngle=4.71239
    g207: ArcOfCircle CenterX=244.625 CenterY=-44.6 CenterZ=0 NormalX=0 NormalY=0 NormalZ=1 AngleXU=0 Radius=0.5 StartAngle=4.71239 EndAngle=6.28319
    g208: LineSegment StartX=260.2 StartY=-31.1 StartZ=0 EndX=273.2 EndY=-31.1 EndZ=0
    g209: LineSegment StartX=260.2 StartY=-45.1 StartZ=0 EndX=273.2 EndY=-45.1 EndZ=0
    g210: LineSegment StartX=259.7 StartY=-31.6 StartZ=0 EndX=259.7 EndY=-44.6 EndZ=0
    g211: LineSegment StartX=273.7 StartY=-31.6 StartZ=0 EndX=273.7 EndY=-44.6 EndZ=0
    g212: ArcOfCircle CenterX=260.2 CenterY=-31.6 CenterZ=0 NormalX=0 NormalY=0 NormalZ=1 AngleXU=0 Radius=0.5 StartAngle=1.5708 EndAngle=3.14159
    g213: ArcOfCircle CenterX=273.2 CenterY=-31.6 CenterZ=0 NormalX=0 NormalY=0 NormalZ=1 AngleXU=0 Radius=0.5 StartAngle=0 EndAngle=1.5708
    g214: ArcOfCircle CenterX=260.2 CenterY=-44.6 CenterZ=0 NormalX=0 NormalY=0 NormalZ=1 AngleXU=0 Radius=0.5 StartAngle=3.14159 EndAngle=4.71239
    g215: ArcOfCircle CenterX=273.2 CenterY=-44.6 CenterZ=0 NormalX=0 NormalY=0 NormalZ=1 AngleXU=0 Radius=0.5 StartAngle=4.71239 EndAngle=6.28319
    g216: LineSegment StartX=251.762 StartY=-32.1 StartZ=0 EndX=257.762 EndY=-32.1 EndZ=0
    g217: LineSegment StartX=251.762 StartY=-47.1 StartZ=0 EndX=257.762 EndY=-47.1 EndZ=0
    g218: LineSegment StartX=251.262 StartY=-32.6 StartZ=0 EndX=251.262 EndY=-46.6 EndZ=0
    g219: LineSegment StartX=258.262 StartY=-32.6 StartZ=0 EndX=258.262 EndY=-46.6 EndZ=0
    g220: ArcOfCircle CenterX=251.762 CenterY=-32.6 CenterZ=0 NormalX=0 NormalY=0 NormalZ=1 AngleXU=0 Radius=0.5 StartAngle=1.5708 EndAngle=3.14159
    g221: ArcOfCircle CenterX=257.762 CenterY=-32.6 CenterZ=0 NormalX=0 NormalY=0 NormalZ=1 AngleXU=0 Radius=0.5 StartAngle=0 EndAngle=1.5708
    g222: ArcOfCircle CenterX=251.762 CenterY=-46.6 CenterZ=0 NormalX=0 NormalY=0 NormalZ=1 AngleXU=0 Radius=0.5 StartAngle=3.14159 EndAngle=4.71239
    g223: ArcOfCircle CenterX=257.762 CenterY=-46.6 CenterZ=0 NormalX=0 NormalY=0 NormalZ=1 AngleXU=0 Radius=0.5 StartAngle=4.71239 EndAngle=6.28319
    g224: LineSegment StartX=275.638 StartY=-32.1 StartZ=0 EndX=281.638 EndY=-32.1 EndZ=0
    g225: LineSegment StartX=275.638 StartY=-47.1 StartZ=0 EndX=281.638 EndY=-47.1 EndZ=0
    g226: LineSegment StartX=275.138 StartY=-32.6 StartZ=0 EndX=275.138 EndY=-46.6 EndZ=0
    g227: LineSegment StartX=282.138 StartY=-32.6 StartZ=0 EndX=282.138 EndY=-46.6 EndZ=0
    g228: ArcOfCircle CenterX=275.638 CenterY=-32.6 CenterZ=0 NormalX=0 NormalY=0 NormalZ=1 AngleXU=0 Radius=0.5 StartAngle=1.5708 EndAngle=3.14159
    g229: ArcOfCircle CenterX=281.638 CenterY=-32.6 CenterZ=0 NormalX=0 NormalY=0 NormalZ=1 AngleXU=0 Radius=0.5 StartAngle=0 EndAngle=1.5708
    g230: ArcOfCircle CenterX=275.638 CenterY=-46.6 CenterZ=0 NormalX=0 NormalY=0 NormalZ=1 AngleXU=0 Radius=0.5 StartAngle=3.14159 EndAngle=4.71239
    g231: ArcOfCircle CenterX=281.638 CenterY=-46.6 CenterZ=0 NormalX=0 NormalY=0 NormalZ=1 AngleXU=0 Radius=0.5 StartAngle=4.71239 EndAngle=6.28319
    g232: LineSegment StartX=293.538 StartY=-31.1 StartZ=0 EndX=306.538 EndY=-31.1 EndZ=0
    g233: LineSegment StartX=293.538 StartY=-45.1 StartZ=0 EndX=306.538 EndY=-45.1 EndZ=0
    g234: LineSegment StartX=293.038 StartY=-31.6 StartZ=0 EndX=293.038 EndY=-44.6 EndZ=0
    g235: LineSegment StartX=307.038 StartY=-31.6 StartZ=0 EndX=307.038 EndY=-44.6 EndZ=0
    g236: ArcOfCircle CenterX=293.538 CenterY=-31.6 CenterZ=0 NormalX=0 NormalY=0 NormalZ=1 AngleXU=0 Radius=0.5 StartAngle=1.5708 EndAngle=3.14159
    g237: ArcOfCircle CenterX=306.538 CenterY=-31.6 CenterZ=0 NormalX=0 NormalY=0 NormalZ=1 AngleXU=0 Radius=0.5 StartAngle=0 EndAngle=1.5708
    g238: ArcOfCircle CenterX=293.538 CenterY=-44.6 CenterZ=0 NormalX=0 NormalY=0 NormalZ=1 AngleXU=0 Radius=0.5 StartAngle=3.14159 EndAngle=4.71239
    g239: ArcOfCircle CenterX=306.538 CenterY=-44.6 CenterZ=0 NormalX=0 NormalY=0 NormalZ=1 AngleXU=0 Radius=0.5 StartAngle=4.71239 EndAngle=6.28319
    g240: LineSegment StartX=317.35 StartY=-31.1 StartZ=0 EndX=330.35 EndY=-31.1 EndZ=0
    g241: LineSegment StartX=317.35 StartY=-45.1 StartZ=0 EndX=330.35 EndY=-45.1 EndZ=0
    g242: LineSegment StartX=316.85 StartY=-31.6 StartZ=0 EndX=316.85 EndY=-44.6 EndZ=0
    g243: LineSegment StartX=330.85 StartY=-31.6 StartZ=0 EndX=330.85 EndY=-44.6 EndZ=0
    g244: ArcOfCircle CenterX=317.35 CenterY=-31.6 CenterZ=0 NormalX=0 NormalY=0 NormalZ=1 AngleXU=0 Radius=0.5 StartAngle=1.5708 EndAngle=3.14159
    g245: ArcOfCircle CenterX=330.35 CenterY=-31.6 CenterZ=0 NormalX=0 NormalY=0 NormalZ=1 AngleXU=0 Radius=0.5 StartAngle=0 EndAngle=1.5708
    g246: ArcOfCircle CenterX=317.35 CenterY=-44.6 CenterZ=0 NormalX=0 NormalY=0 NormalZ=1 AngleXU=0 Radius=0.5 StartAngle=3.14159 EndAngle=4.71239
    g247: ArcOfCircle CenterX=330.35 CenterY=-44.6 CenterZ=0 NormalX=0 NormalY=0 NormalZ=1 AngleXU=0 Radius=0.5 StartAngle=4.71239 EndAngle=6.28319
    g248: LineSegment StartX=336.4 StartY=-31.1 StartZ=0 EndX=349.4 EndY=-31.1 EndZ=0
    g249: LineSegment StartX=336.4 StartY=-45.1 StartZ=0 EndX=349.4 EndY=-45.1 EndZ=0
    g250: LineSegment StartX=335.9 StartY=-31.6 StartZ=0 EndX=335.9 EndY=-44.6 EndZ=0
    g251: LineSegment StartX=349.9 StartY=-31.6 StartZ=0 EndX=349.9 EndY=-44.6 EndZ=0
    g252: ArcOfCircle CenterX=336.4 CenterY=-31.6 CenterZ=0 NormalX=0 NormalY=0 NormalZ=1 AngleXU=0 Radius=0.5 StartAngle=1.5708 EndAngle=3.14159
    g253: ArcOfCircle CenterX=349.4 CenterY=-31.6 CenterZ=0 NormalX=0 NormalY=0 NormalZ=1 AngleXU=0 Radius=0.5 StartAngle=0 EndAngle=1.5708
    g254: ArcOfCircle CenterX=336.4 CenterY=-44.6 CenterZ=0 NormalX=0 NormalY=0 NormalZ=1 AngleXU=0 Radius=0.5 StartAngle=3.14159 EndAngle=4.71239
    g255: ArcOfCircle CenterX=349.4 CenterY=-44.6 CenterZ=0 NormalX=0 NormalY=0 NormalZ=1 AngleXU=0 Radius=0.5 StartAngle=4.71239 EndAngle=6.28319
    g256: LineSegment StartX=355.45 StartY=-31.1 StartZ=0 EndX=368.45 EndY=-31.1 EndZ=0
    g257: LineSegment StartX=355.45 StartY=-45.1 StartZ=0 EndX=368.45 EndY=-45.1 EndZ=0
    g258: LineSegment StartX=354.95 StartY=-31.6 StartZ=0 EndX=354.95 EndY=-44.6 EndZ=0
    g259: LineSegment StartX=368.95 StartY=-31.6 StartZ=0 EndX=368.95 EndY=-44.6 EndZ=0
    g260: ArcOfCircle CenterX=355.45 CenterY=-31.6 CenterZ=0 NormalX=0 NormalY=0 NormalZ=1 AngleXU=0 Radius=0.5 StartAngle=1.5708 EndAngle=3.14159
    g261: ArcOfCircle CenterX=368.45 CenterY=-31.6 CenterZ=0 NormalX=0 NormalY=0 NormalZ=1 AngleXU=0 Radius=0.5 StartAngle=0 EndAngle=1.5708
    g262: ArcOfCircle CenterX=355.45 CenterY=-44.6 CenterZ=0 NormalX=0 NormalY=0 NormalZ=1 AngleXU=0 Radius=0.5 StartAngle=3.14159 EndAngle=4.71239
    g263: ArcOfCircle CenterX=368.45 CenterY=-44.6 CenterZ=0 NormalX=0 NormalY=0 NormalZ=1 AngleXU=0 Radius=0.5 StartAngle=4.71239 EndAngle=6.28319
    g264: LineSegment StartX=374.5 StartY=-31.1 StartZ=0 EndX=387.5 EndY=-31.1 EndZ=0
    g265: LineSegment StartX=374.5 StartY=-45.1 StartZ=0 EndX=387.5 EndY=-45.1 EndZ=0
    g266: LineSegment StartX=374 StartY=-31.6 StartZ=0 EndX=374 EndY=-44.6 EndZ=0
    g267: LineSegment StartX=388 StartY=-31.6 StartZ=0 EndX=388 EndY=-44.6 EndZ=0
    g268: ArcOfCircle CenterX=374.5 CenterY=-31.6 CenterZ=0 NormalX=0 NormalY=0 NormalZ=1 AngleXU=0 Radius=0.5 StartAngle=1.5708 EndAngle=3.14159
    g269: ArcOfCircle CenterX=387.5 CenterY=-31.6 CenterZ=0 NormalX=0 NormalY=0 NormalZ=1 AngleXU=0 Radius=0.5 StartAngle=0 EndAngle=1.5708
    g270: ArcOfCircle CenterX=374.5 CenterY=-44.6 CenterZ=0 NormalX=0 NormalY=0 NormalZ=1 AngleXU=0 Radius=0.5 StartAngle=3.14159 EndAngle=4.71239
    g271: ArcOfCircle CenterX=387.5 CenterY=-44.6 CenterZ=0 NormalX=0 NormalY=0 NormalZ=1 AngleXU=0 Radius=0.5 StartAngle=4.71239 EndAngle=6.28319
    g272: LineSegment StartX=7.7875 StartY=-50.15 StartZ=0 EndX=20.7875 EndY=-50.15 EndZ=0
    g273: LineSegment StartX=7.7875 StartY=-64.15 StartZ=0 EndX=20.7875 EndY=-64.15 EndZ=0
    g274: LineSegment StartX=7.2875 StartY=-50.65 StartZ=0 EndX=7.2875 EndY=-63.65 EndZ=0
    g275: LineSegment StartX=21.2875 StartY=-50.65 StartZ=0 EndX=21.2875 EndY=-63.65 EndZ=0
    g276: ArcOfCircle CenterX=7.7875 CenterY=-50.65 CenterZ=0 NormalX=0 NormalY=0 NormalZ=1 AngleXU=0 Radius=0.5 StartAngle=1.5708 EndAngle=3.14159
    g277: ArcOfCircle CenterX=20.7875 CenterY=-50.65 CenterZ=0 NormalX=0 NormalY=0 NormalZ=1 AngleXU=0 Radius=0.5 StartAngle=0 EndAngle=1.5708
    g278: ArcOfCircle CenterX=7.7875 CenterY=-63.65 CenterZ=0 NormalX=0 NormalY=0 NormalZ=1 AngleXU=0 Radius=0.5 StartAngle=3.14159 EndAngle=4.71239
    g279: ArcOfCircle CenterX=20.7875 CenterY=-63.65 CenterZ=0 NormalX=0 NormalY=0 NormalZ=1 AngleXU=0 Radius=0.5 StartAngle=4.71239 EndAngle=6.28319
    g280: LineSegment StartX=31.6 StartY=-50.15 StartZ=0 EndX=44.6 EndY=-50.15 EndZ=0
    g281: LineSegment StartX=31.6 StartY=-64.15 StartZ=0 EndX=44.6 EndY=-64.15 EndZ=0
    g282: LineSegment StartX=31.1 StartY=-50.65 StartZ=0 EndX=31.1 EndY=-63.65 EndZ=0
    g283: LineSegment StartX=45.1 StartY=-50.65 StartZ=0 EndX=45.1 EndY=-63.65 EndZ=0
    g284: ArcOfCircle CenterX=31.6 CenterY=-50.65 CenterZ=0 NormalX=0 NormalY=0 NormalZ=1 AngleXU=0 Radius=0.5 StartAngle=1.5708 EndAngle=3.14159
    g285: ArcOfCircle CenterX=44.6 CenterY=-50.65 CenterZ=0 NormalX=0 NormalY=0 NormalZ=1 AngleXU=0 Radius=0.5 StartAngle=0 EndAngle=1.5708
    g286: ArcOfCircle CenterX=31.6 CenterY=-63.65 CenterZ=0 NormalX=0 NormalY=0 NormalZ=1 AngleXU=0 Radius=0.5 StartAngle=3.14159 EndAngle=4.71239
    g287: ArcOfCircle CenterX=44.6 CenterY=-63.65 CenterZ=0 NormalX=0 NormalY=0 NormalZ=1 AngleXU=0 Radius=0.5 StartAngle=4.71239 EndAngle=6.28319
    g288: LineSegment StartX=50.65 StartY=-50.15 StartZ=0 EndX=63.65 EndY=-50.15 EndZ=0
    g289: LineSegment StartX=50.65 StartY=-64.15 StartZ=0 EndX=63.65 EndY=-64.15 EndZ=0
    g290: LineSegment StartX=50.15 StartY=-50.65 StartZ=0 EndX=50.15 EndY=-63.65 EndZ=0
    g291: LineSegment StartX=64.15 StartY=-50.65 StartZ=0 EndX=64.15 EndY=-63.65 EndZ=0
    g292: ArcOfCircle CenterX=50.65 CenterY=-50.65 CenterZ=0 NormalX=0 NormalY=0 NormalZ=1 AngleXU=0 Radius=0.5 StartAngle=1.5708 EndAngle=3.14159
    g293: ArcOfCircle CenterX=63.65 CenterY=-50.65 CenterZ=0 NormalX=0 NormalY=0 NormalZ=1 AngleXU=0 Radius=0.5 StartAngle=0 EndAngle=1.5708
    g294: ArcOfCircle CenterX=50.65 CenterY=-63.65 CenterZ=0 NormalX=0 NormalY=0 NormalZ=1 AngleXU=0 Radius=0.5 StartAngle=3.14159 EndAngle=4.71239
    g295: ArcOfCircle CenterX=63.65 CenterY=-63.65 CenterZ=0 NormalX=0 NormalY=0 NormalZ=1 AngleXU=0 Radius=0.5 StartAngle=4.71239 EndAngle=6.28319
    g296: LineSegment StartX=69.7 StartY=-50.15 StartZ=0 EndX=82.7 EndY=-50.15 EndZ=0
    g297: LineSegment StartX=69.7 StartY=-64.15 StartZ=0 EndX=82.7 EndY=-64.15 EndZ=0
    g298: LineSegment StartX=69.2 StartY=-50.65 StartZ=0 EndX=69.2 EndY=-63.65 EndZ=0
    g299: LineSegment StartX=83.2 StartY=-50.65 StartZ=0 EndX=83.2 EndY=-63.65 EndZ=0
    g300: ArcOfCircle CenterX=69.7 CenterY=-50.65 CenterZ=0 NormalX=0 NormalY=0 NormalZ=1 AngleXU=0 Radius=0.5 StartAngle=1.5708 EndAngle=3.14159
    g301: ArcOfCircle CenterX=82.7 CenterY=-50.65 CenterZ=0 NormalX=0 NormalY=0 NormalZ=1 AngleXU=0 Radius=0.5 StartAngle=0 EndAngle=1.5708
    g302: ArcOfCircle CenterX=69.7 CenterY=-63.65 CenterZ=0 NormalX=0 NormalY=0 NormalZ=1 AngleXU=0 Radius=0.5 StartAngle=3.14159 EndAngle=4.71239
    g303: ArcOfCircle CenterX=82.7 CenterY=-63.65 CenterZ=0 NormalX=0 NormalY=0 NormalZ=1 AngleXU=0 Radius=0.5 StartAngle=4.71239 EndAngle=6.28319
    g304: LineSegment StartX=88.75 StartY=-50.15 StartZ=0 EndX=101.75 EndY=-50.15 EndZ=0
    g305: LineSegment StartX=88.75 StartY=-64.15 StartZ=0 EndX=101.75 EndY=-64.15 EndZ=0
    g306: LineSegment StartX=88.25 StartY=-50.65 StartZ=0 EndX=88.25 EndY=-63.65 EndZ=0
    g307: LineSegment StartX=102.25 StartY=-50.65 StartZ=0 EndX=102.25 EndY=-63.65 EndZ=0
    g308: ArcOfCircle CenterX=88.75 CenterY=-50.65 CenterZ=0 NormalX=0 NormalY=0 NormalZ=1 AngleXU=0 Radius=0.5 StartAngle=1.5708 EndAngle=3.14159
    g309: ArcOfCircle CenterX=101.75 CenterY=-50.65 CenterZ=0 NormalX=0 NormalY=0 NormalZ=1 AngleXU=0 Radius=0.5 StartAngle=0 EndAngle=1.5708
    g310: ArcOfCircle CenterX=88.75 CenterY=-63.65 CenterZ=0 NormalX=0 NormalY=0 NormalZ=1 AngleXU=0 Radius=0.5 StartAngle=3.14159 EndAngle=4.71239
    g311: ArcOfCircle CenterX=101.75 CenterY=-63.65 CenterZ=0 NormalX=0 NormalY=0 NormalZ=1 AngleXU=0 Radius=0.5 StartAngle=4.71239 EndAngle=6.28319
    g312: LineSegment StartX=107.8 StartY=-50.15 StartZ=0 EndX=120.8 EndY=-50.15 EndZ=0
    g313: LineSegment StartX=107.8 StartY=-64.15 StartZ=0 EndX=120.8 EndY=-64.15 EndZ=0
    g314: LineSegment StartX=107.3 StartY=-50.65 StartZ=0 EndX=107.3 EndY=-63.65 EndZ=0
    g315: LineSegment StartX=121.3 StartY=-50.65 StartZ=0 EndX=121.3 EndY=-63.65 EndZ=0
    g316: ArcOfCircle CenterX=107.8 CenterY=-50.65 CenterZ=0 NormalX=0 NormalY=0 NormalZ=1 AngleXU=0 Radius=0.5 StartAngle=1.5708 EndAngle=3.14159
    g317: ArcOfCircle CenterX=120.8 CenterY=-50.65 CenterZ=0 NormalX=0 NormalY=0 NormalZ=1 AngleXU=0 Radius=0.5 StartAngle=0 EndAngle=1.5708
    g318: ArcOfCircle CenterX=107.8 CenterY=-63.65 CenterZ=0 NormalX=0 NormalY=0 NormalZ=1 AngleXU=0 Radius=0.5 StartAngle=3.14159 EndAngle=4.71239
    g319: ArcOfCircle CenterX=120.8 CenterY=-63.65 CenterZ=0 NormalX=0 NormalY=0 NormalZ=1 AngleXU=0 Radius=0.5 StartAngle=4.71239 EndAngle=6.28319
    g320: LineSegment StartX=126.85 StartY=-50.15 StartZ=0 EndX=139.85 EndY=-50.15 EndZ=0
    g321: LineSegment StartX=126.85 StartY=-64.15 StartZ=0 EndX=139.85 EndY=-64.15 EndZ=0
    g322: LineSegment StartX=126.35 StartY=-50.65 StartZ=0 EndX=126.35 EndY=-63.65 EndZ=0
    g323: LineSegment StartX=140.35 StartY=-50.65 StartZ=0 EndX=140.35 EndY=-63.65 EndZ=0
    g324: ArcOfCircle CenterX=126.85 CenterY=-50.65 CenterZ=0 NormalX=0 NormalY=0 NormalZ=1 AngleXU=0 Radius=0.5 StartAngle=1.5708 EndAngle=3.14159
    g325: ArcOfCircle CenterX=139.85 CenterY=-50.65 CenterZ=0 NormalX=0 NormalY=0 NormalZ=1 AngleXU=0 Radius=0.5 StartAngle=0 EndAngle=1.5708
    g326: ArcOfCircle CenterX=126.85 CenterY=-63.65 CenterZ=0 NormalX=0 NormalY=0 NormalZ=1 AngleXU=0 Radius=0.5 StartAngle=3.14159 EndAngle=4.71239
    g327: ArcOfCircle CenterX=139.85 CenterY=-63.65 CenterZ=0 NormalX=0 NormalY=0 NormalZ=1 AngleXU=0 Radius=0.5 StartAngle=4.71239 EndAngle=6.28319
    g328: LineSegment StartX=145.9 StartY=-50.15 StartZ=0 EndX=158.9 EndY=-50.15 EndZ=0
    g329: LineSegment StartX=145.9 StartY=-64.15 StartZ=0 EndX=158.9 EndY=-64.15 EndZ=0
    g330: LineSegment StartX=145.4 StartY=-50.65 StartZ=0 EndX=145.4 EndY=-63.65 EndZ=0
    g331: LineSegment StartX=159.4 StartY=-50.65 StartZ=0 EndX=159.4 EndY=-63.65 EndZ=0
    g332: ArcOfCircle CenterX=145.9 CenterY=-50.65 CenterZ=0 NormalX=0 NormalY=0 NormalZ=1 AngleXU=0 Radius=0.5 StartAngle=1.5708 EndAngle=3.14159
    g333: ArcOfCircle CenterX=158.9 CenterY=-50.65 CenterZ=0 NormalX=0 NormalY=0 NormalZ=1 AngleXU=0 Radius=0.5 StartAngle=0 EndAngle=1.5708
    g334: ArcOfCircle CenterX=145.9 CenterY=-63.65 CenterZ=0 NormalX=0 NormalY=0 NormalZ=1 AngleXU=0 Radius=0.5 StartAngle=3.14159 EndAngle=4.71239
    g335: ArcOfCircle CenterX=158.9 CenterY=-63.65 CenterZ=0 NormalX=0 NormalY=0 NormalZ=1 AngleXU=0 Radius=0.5 StartAngle=4.71239 EndAngle=6.28319
    g336: LineSegment StartX=164.95 StartY=-50.15 StartZ=0 EndX=177.95 EndY=-50.15 EndZ=0
    g337: LineSegment StartX=164.95 StartY=-64.15 StartZ=0 EndX=177.95 EndY=-64.15 EndZ=0
    g338: LineSegment StartX=164.45 StartY=-50.65 StartZ=0 EndX=164.45 EndY=-63.65 EndZ=0
    g339: LineSegment StartX=178.45 StartY=-50.65 StartZ=0 EndX=178.45 EndY=-63.65 EndZ=0
    g340: ArcOfCircle CenterX=164.95 CenterY=-50.65 CenterZ=0 NormalX=0 NormalY=0 NormalZ=1 AngleXU=0 Radius=0.5 StartAngle=1.5708 EndAngle=3.14159
    g341: ArcOfCircle CenterX=177.95 CenterY=-50.65 CenterZ=0 NormalX=0 NormalY=0 NormalZ=1 AngleXU=0 Radius=0.5 StartAngle=0 EndAngle=1.5708
    g342: ArcOfCircle CenterX=164.95 CenterY=-63.65 CenterZ=0 NormalX=0 NormalY=0 NormalZ=1 AngleXU=0 Radius=0.5 StartAngle=3.14159 EndAngle=4.71239
    g343: ArcOfCircle CenterX=177.95 CenterY=-63.65 CenterZ=0 NormalX=0 NormalY=0 NormalZ=1 AngleXU=0 Radius=0.5 StartAngle=4.71239 EndAngle=6.28319
    g344: LineSegment StartX=184 StartY=-50.15 StartZ=0 EndX=197 EndY=-50.15 EndZ=0
    g345: LineSegment StartX=184 StartY=-64.15 StartZ=0 EndX=197 EndY=-64.15 EndZ=0
    g346: LineSegment StartX=183.5 StartY=-50.65 StartZ=0 EndX=183.5 EndY=-63.65 EndZ=0
    g347: LineSegment StartX=197.5 StartY=-50.65 StartZ=0 EndX=197.5 EndY=-63.65 EndZ=0
    g348: ArcOfCircle CenterX=184 CenterY=-50.65 CenterZ=0 NormalX=0 NormalY=0 NormalZ=1 AngleXU=0 Radius=0.5 StartAngle=1.5708 EndAngle=3.14159
    g349: ArcOfCircle CenterX=197 CenterY=-50.65 CenterZ=0 NormalX=0 NormalY=0 NormalZ=1 AngleXU=0 Radius=0.5 StartAngle=0 EndAngle=1.5708
    g350: ArcOfCircle CenterX=184 CenterY=-63.65 CenterZ=0 NormalX=0 NormalY=0 NormalZ=1 AngleXU=0 Radius=0.5 StartAngle=3.14159 EndAngle=4.71239
    g351: ArcOfCircle CenterX=197 CenterY=-63.65 CenterZ=0 NormalX=0 NormalY=0 NormalZ=1 AngleXU=0 Radius=0.5 StartAngle=4.71239 EndAngle=6.28319
    g352: LineSegment StartX=203.05 StartY=-50.15 StartZ=0 EndX=216.05 EndY=-50.15 EndZ=0
    g353: LineSegment StartX=203.05 StartY=-64.15 StartZ=0 EndX=216.05 EndY=-64.15 EndZ=0
    g354: LineSegment StartX=202.55 StartY=-50.65 StartZ=0 EndX=202.55 EndY=-63.65 EndZ=0
    g355: LineSegment StartX=216.55 StartY=-50.65 StartZ=0 EndX=216.55 EndY=-63.65 EndZ=0
    g356: ArcOfCircle CenterX=203.05 CenterY=-50.65 CenterZ=0 NormalX=0 NormalY=0 NormalZ=1 AngleXU=0 Radius=0.5 StartAngle=1.5708 EndAngle=3.14159
    g357: ArcOfCircle CenterX=216.05 CenterY=-50.65 CenterZ=0 NormalX=0 NormalY=0 NormalZ=1 AngleXU=0 Radius=0.5 StartAngle=0 EndAngle=1.5708
    g358: ArcOfCircle CenterX=203.05 CenterY=-63.65 CenterZ=0 NormalX=0 NormalY=0 NormalZ=1 AngleXU=0 Radius=0.5 StartAngle=3.14159 EndAngle=4.71239
    g359: ArcOfCircle CenterX=216.05 CenterY=-63.65 CenterZ=0 NormalX=0 NormalY=0 NormalZ=1 AngleXU=0 Radius=0.5 StartAngle=4.71239 EndAngle=6.28319
    g360: LineSegment StartX=222.1 StartY=-50.15 StartZ=0 EndX=235.1 EndY=-50.15 EndZ=0
    g361: LineSegment StartX=222.1 StartY=-64.15 StartZ=0 EndX=235.1 EndY=-64.15 EndZ=0
    g362: LineSegment StartX=221.6 StartY=-50.65 StartZ=0 EndX=221.6 EndY=-63.65 EndZ=0
    g363: LineSegment StartX=235.6 StartY=-50.65 StartZ=0 EndX=235.6 EndY=-63.65 EndZ=0
    g364: ArcOfCircle CenterX=222.1 CenterY=-50.65 CenterZ=0 NormalX=0 NormalY=0 NormalZ=1 AngleXU=0 Radius=0.5 StartAngle=1.5708 EndAngle=3.14159
    g365: ArcOfCircle CenterX=235.1 CenterY=-50.65 CenterZ=0 NormalX=0 NormalY=0 NormalZ=1 AngleXU=0 Radius=0.5 StartAngle=0 EndAngle=1.5708
    g366: ArcOfCircle CenterX=222.1 CenterY=-63.65 CenterZ=0 NormalX=0 NormalY=0 NormalZ=1 AngleXU=0 Radius=0.5 StartAngle=3.14159 EndAngle=4.71239
    g367: ArcOfCircle CenterX=235.1 CenterY=-63.65 CenterZ=0 NormalX=0 NormalY=0 NormalZ=1 AngleXU=0 Radius=0.5 StartAngle=4.71239 EndAngle=6.28319
    g368: LineSegment StartX=241.15 StartY=-50.15 StartZ=0 EndX=254.15 EndY=-50.15 EndZ=0
    g369: LineSegment StartX=241.15 StartY=-64.15 StartZ=0 EndX=254.15 EndY=-64.15 EndZ=0
    g370: LineSegment StartX=240.65 StartY=-50.65 StartZ=0 EndX=240.65 EndY=-63.65 EndZ=0
    g371: LineSegment StartX=254.65 StartY=-50.65 StartZ=0 EndX=254.65 EndY=-63.65 EndZ=0
    g372: ArcOfCircle CenterX=241.15 CenterY=-50.65 CenterZ=0 NormalX=0 NormalY=0 NormalZ=1 AngleXU=0 Radius=0.5 StartAngle=1.5708 EndAngle=3.14159
    g373: ArcOfCircle CenterX=254.15 CenterY=-50.65 CenterZ=0 NormalX=0 NormalY=0 NormalZ=1 AngleXU=0 Radius=0.5 StartAngle=0 EndAngle=1.5708
    g374: ArcOfCircle CenterX=241.15 CenterY=-63.65 CenterZ=0 NormalX=0 NormalY=0 NormalZ=1 AngleXU=0 Radius=0.5 StartAngle=3.14159 EndAngle=4.71239
    g375: ArcOfCircle CenterX=254.15 CenterY=-63.65 CenterZ=0 NormalX=0 NormalY=0 NormalZ=1 AngleXU=0 Radius=0.5 StartAngle=4.71239 EndAngle=6.28319
    g376: LineSegment StartX=264.962 StartY=-50.15 StartZ=0 EndX=277.962 EndY=-50.15 EndZ=0
    g377: LineSegment StartX=264.962 StartY=-64.15 StartZ=0 EndX=277.962 EndY=-64.15 EndZ=0
    g378: LineSegment StartX=264.462 StartY=-50.65 StartZ=0 EndX=264.462 EndY=-63.65 EndZ=0
    g379: LineSegment StartX=278.462 StartY=-50.65 StartZ=0 EndX=278.462 EndY=-63.65 EndZ=0
    g380: ArcOfCircle CenterX=264.962 CenterY=-50.65 CenterZ=0 NormalX=0 NormalY=0 NormalZ=1 AngleXU=0 Radius=0.5 StartAngle=1.5708 EndAngle=3.14159
    g381: ArcOfCircle CenterX=277.962 CenterY=-50.65 CenterZ=0 NormalX=0 NormalY=0 NormalZ=1 AngleXU=0 Radius=0.5 StartAngle=0 EndAngle=1.5708
    g382: ArcOfCircle CenterX=264.962 CenterY=-63.65 CenterZ=0 NormalX=0 NormalY=0 NormalZ=1 AngleXU=0 Radius=0.5 StartAngle=3.14159 EndAngle=4.71239
    g383: ArcOfCircle CenterX=277.962 CenterY=-63.65 CenterZ=0 NormalX=0 NormalY=0 NormalZ=1 AngleXU=0 Radius=0.5 StartAngle=4.71239 EndAngle=6.28319
    g384: LineSegment StartX=293.538 StartY=-50.15 StartZ=0 EndX=306.538 EndY=-50.15 EndZ=0
    g385: LineSegment StartX=293.538 StartY=-64.15 StartZ=0 EndX=306.538 EndY=-64.15 EndZ=0
    g386: LineSegment StartX=293.038 StartY=-50.65 StartZ=0 EndX=293.038 EndY=-63.65 EndZ=0
    g387: LineSegment StartX=307.038 StartY=-50.65 StartZ=0 EndX=307.038 EndY=-63.65 EndZ=0
    g388: ArcOfCircle CenterX=293.538 CenterY=-50.65 CenterZ=0 NormalX=0 NormalY=0 NormalZ=1 AngleXU=0 Radius=0.5 StartAngle=1.5708 EndAngle=3.14159
    g389: ArcOfCircle CenterX=306.538 CenterY=-50.65 CenterZ=0 NormalX=0 NormalY=0 NormalZ=1 AngleXU=0 Radius=0.5 StartAngle=0 EndAngle=1.5708
    g390: ArcOfCircle CenterX=293.538 CenterY=-63.65 CenterZ=0 NormalX=0 NormalY=0 NormalZ=1 AngleXU=0 Radius=0.5 StartAngle=3.14159 EndAngle=4.71239
    g391: ArcOfCircle CenterX=306.538 CenterY=-63.65 CenterZ=0 NormalX=0 NormalY=0 NormalZ=1 AngleXU=0 Radius=0.5 StartAngle=4.71239 EndAngle=6.28319
    g392: LineSegment StartX=317.35 StartY=-50.15 StartZ=0 EndX=330.35 EndY=-50.15 EndZ=0
    g393: LineSegment StartX=317.35 StartY=-64.15 StartZ=0 EndX=330.35 EndY=-64.15 EndZ=0
    g394: LineSegment StartX=316.85 StartY=-50.65 StartZ=0 EndX=316.85 EndY=-63.65 EndZ=0
    g395: LineSegment StartX=330.85 StartY=-50.65 StartZ=0 EndX=330.85 EndY=-63.65 EndZ=0
    g396: ArcOfCircle CenterX=317.35 CenterY=-50.65 CenterZ=0 NormalX=0 NormalY=0 NormalZ=1 AngleXU=0 Radius=0.5 StartAngle=1.5708 EndAngle=3.14159
    g397: ArcOfCircle CenterX=330.35 CenterY=-50.65 CenterZ=0 NormalX=0 NormalY=0 NormalZ=1 AngleXU=0 Radius=0.5 StartAngle=0 EndAngle=1.5708
    g398: ArcOfCircle CenterX=317.35 CenterY=-63.65 CenterZ=0 NormalX=0 NormalY=0 NormalZ=1 AngleXU=0 Radius=0.5 StartAngle=3.14159 EndAngle=4.71239
    g399: ArcOfCircle CenterX=330.35 CenterY=-63.65 CenterZ=0 NormalX=0 NormalY=0 NormalZ=1 AngleXU=0 Radius=0.5 StartAngle=4.71239 EndAngle=6.28319
    ... +534 more geometry lines
  constraints (969):
    c: Block(g0)
    c: Block(g1)
    c: Block(g2)
    c: Block(g3)
    c: Block(g4)
    c: Block(g5)
    c: Block(g6)
    c: Block(g7)
    c: Block(g8)
    c: Block(g9)
    c: Block(g10)
    c: Block(g11)
    c: Block(g12)
    c: Block(g13)
    c: Block(g14)
    c: Block(g15)
    c: Block(g16)
    c: Block(g17)
    c: Block(g18)
    c: Block(g19)
    c: Block(g20)
    c: Block(g21)
    c: Block(g22)
    c: Block(g23)
    c: Block(g24)
    c: Block(g25)
    c: Block(g26)
    c: Block(g27)
    c: Block(g28)
    c: Block(g29)
    c: Block(g30)
    c: Block(g31)
    c: Block(g32)
    c: Block(g33)
    c: Block(g34)
    c: Block(g35)
    c: Block(g36)
    c: Block(g37)
    c: Block(g38)
    c: Block(g39)
    c: Block(g40)
    c: Block(g41)
    c: Block(g42)
    c: Block(g43)
    c: Block(g44)
    c: Diameter(g920) = 4
    c: DistanceX(g920,g2) = 4.693
    c: DistanceY(g0,g920) = 9.491
    c: Equal(g921,g920)
    c: Horizontal(g921,g920)
    c: DistanceX(g920,g921) = 397.51
    c: Equal(g921,g922)
    c: Vertical(g921,g922)
    c: DistanceY(g922,g921) = 129.758
    c: Equal(g923,g922)
    c: Horizontal(g922,g923)
    c: Vertical(g923,g920)
    c: Equal(g924,g921)
    c: DistanceY(g924,g921) = 1.275
    c: DistanceX(g924,g921) = 190.505
    c: Equal(g925,g922)
    c: DistanceY(g925,g923) = 1.19
    c: DistanceX(g923,g925) = 203.19
    c: Block(g45)
    c: Block(g46)
    c: Block(g47)
    c: Block(g48)
    c: Block(g49)
    c: Block(g50)
    c: Block(g51)
    c: Block(g52)
    c: Block(g53)
    c: Block(g54)
    c: Block(g55)
    c: Block(g56)
    c: Block(g57)
    c: Block(g58)
    c: Block(g59)
    c: Block(g60)
    c: Block(g61)
    c: Block(g62)
    c: Block(g63)
    c: Block(g64)
    c: Block(g65)
    c: Block(g66)
    c: Block(g67)
    c: Block(g68)
    c: Block(g69)
    c: Block(g70)
    c: Block(g71)
    c: Block(g72)
    c: Block(g73)
    c: Block(g74)
    c: Block(g75)
    c: Block(g76)
    c: Block(g77)
    c: Block(g78)
    c: Block(g79)
    c: Block(g80)
    c: Block(g81)
    c: Block(g82)
    c: Block(g83)
    c: Block(g84)
    c: Block(g85)
    c: Block(g86)
    c: Block(g87)
    c: Block(g88)
    c: Block(g89)
    c: Block(g90)
    c: Block(g91)
    c: Block(g92)
    c: Block(g93)
    c: Block(g94)
    c: Block(g95)
    c: Block(g96)
    c: Block(g97)
    c: Block(g98)
    c: Block(g99)
    c: Block(g100)
    c: Block(g101)
    c: Block(g102)
    c: Block(g103)
    c: Block(g104)
    c: Block(g105)
    c: Block(g106)
    c: Block(g107)
    c: Block(g108)
    c: Block(g109)
    c: Block(g110)
    c: Block(g111)
    c: Block(g112)
    c: Block(g113)
    c: Block(g114)
    c: Block(g115)
    c: Block(g116)
    c: Block(g117)
    c: Block(g118)
    c: Block(g119)
    c: Block(g120)
    c: Block(g121)
    c: Block(g122)
    c: Block(g123)
    c: Block(g124)
    c: Block(g125)
    c: Block(g126)
    c: Block(g127)
    c: Block(g128)
    c: Block(g129)
    c: Block(g130)
    c: Block(g131)
    c: Block(g132)
    c: Block(g133)
    c: Block(g134)
    c: Block(g135)
    c: Block(g136)
    c: Block(g137)
    c: Block(g138)
    c: Block(g139)
    c: Block(g140)
    c: Block(g141)
    c: Block(g142)
    c: Block(g143)
    c: Block(g144)
    c: Block(g145)
    c: Block(g146)
    c: Block(g147)
    c: Block(g148)
    c: Block(g149)
    c: Block(g150)
    c: Block(g151)
    c: Block(g152)
    c: Block(g153)
    c: Block(g154)
    c: Block(g155)
    c: Block(g156)
    c: Block(g157)
    c: Block(g158)
    c: Block(g159)
    c: Block(g160)
    c: Block(g161)
    c: Block(g162)
    c: Block(g163)
    c: Block(g164)
    c: Block(g165)
    c: Block(g166)
    c: Block(g167)
    c: Block(g168)
    c: Block(g169)
    c: Block(g170)
    c: Block(g171)
    c: Block(g172)
    c: Block(g173)
    c: Block(g174)
    c: Block(g175)
    c: Block(g176)
    c: Block(g177)
    c: Block(g178)
    c: Block(g179)
    c: Block(g180)
    c: Block(g181)
    c: Block(g182)
    c: Block(g183)
    c: Block(g184)
    c: Block(g185)
    c: Block(g186)
    c: Block(g187)
    c: Block(g188)
    c: Block(g189)
    c: Block(g190)
    c: Block(g191)
    c: Block(g192)
    c: Block(g193)
    c: Block(g194)
    c: Block(g195)
    c: Block(g196)
    c: Block(g197)
    c: Block(g198)
    c: Block(g199)
    c: Block(g200)
    c: Block(g201)
    c: Block(g202)
    c: Block(g203)
    c: Block(g204)
    c: Block(g205)
    c: Block(g206)
    c: Block(g207)
    c: Block(g208)
    c: Block(g209)
    c: Block(g210)
    c: Block(g211)
    c: Block(g212)
    c: Block(g213)
    c: Block(g214)
    c: Block(g215)
    c: Block(g216)
    c: Block(g217)
    c: Block(g218)
    c: Block(g219)
    c: Block(g220)
    c: Block(g221)
    c: Block(g222)
    c: Block(g223)
    c: Block(g224)
    c: Block(g225)
    c: Block(g226)
    c: Block(g227)
    c: Block(g228)
    c: Block(g229)
    c: Block(g230)
    c: Block(g231)
    c: Block(g232)
    c: Block(g233)
    c: Block(g234)
    c: Block(g235)
    c: Block(g236)
    c: Block(g237)
    c: Block(g238)
    c: Block(g239)
    c: Block(g240)
    c: Block(g241)
    c: Block(g242)
    c: Block(g243)
    c: Block(g244)
    c: Block(g245)
    c: Block(g246)
    c: Block(g247)
    c: Block(g248)
    c: Block(g249)
    c: Block(g250)
    c: Block(g251)
    c: Block(g252)
    c: Block(g253)
    c: Block(g254)
    c: Block(g255)
    c: Block(g256)
    c: Block(g257)
    c: Block(g258)
    c: Block(g259)
    c: Block(g260)
    c: Block(g261)
    c: Block(g262)
    c: Block(g263)
    c: Block(g264)
    c: Block(g265)
    c: Block(g266)
    c: Block(g267)
    c: Block(g268)
    c: Block(g269)
    c: Block(g270)
    c: Block(g271)
    c: Block(g272)
    c: Block(g273)
    c: Block(g274)
    c: Block(g275)
    c: Block(g276)
    c: Block(g277)
    c: Block(g278)
    c: Block(g279)
    c: Block(g280)
    c: Block(g281)
    c: Block(g282)
    c: Block(g283)
    c: Block(g284)
    c: Block(g285)
    c: Block(g286)
    c: Block(g287)
    c: Block(g288)
    c: Block(g289)
    c: Block(g290)
    c: Block(g291)
    c: Block(g292)
    c: Block(g293)
    c: Block(g294)
    c: Block(g295)
    c: Block(g296)
    c: Block(g297)
    c: Block(g298)
    c: Block(g299)
    c: Block(g300)
    c: Block(g301)
    c: Block(g302)
    c: Block(g303)
    c: Block(g304)
    c: Block(g305)
    c: Block(g306)
    c: Block(g307)
    c: Block(g308)
    c: Block(g309)
    c: Block(g310)
    c: Block(g311)
    c: Block(g312)
    c: Block(g313)
    c: Block(g314)
    c: Block(g315)
    c: Block(g316)
    c: Block(g317)
    c: Block(g318)
    c: Block(g319)
    c: Block(g320)
    c: Block(g321)
    c: Block(g322)
    c: Block(g323)
    c: Block(g324)
    c: Block(g325)
    c: Block(g326)
    c: Block(g327)
    c: Block(g328)
    c: Block(g329)
    c: Block(g330)
    c: Block(g331)
    c: Block(g332)
    c: Block(g333)
    c: Block(g334)
    c: Block(g335)
    c: Block(g336)
    c: Block(g337)
    c: Block(g338)
    c: Block(g339)
    c: Block(g340)
    c: Block(g341)
    c: Block(g342)
    c: Block(g343)
    c: Block(g344)
    c: Block(g345)
    c: Block(g346)
    c: Block(g347)
    c: Block(g348)
    c: Block(g349)
    c: Block(g350)
    c: Block(g351)
    c: Block(g352)
    c: Block(g353)
    c: Block(g354)
    c: Block(g355)
    c: Block(g356)
    c: Block(g357)
    c: Block(g358)
    c: Block(g359)
    c: Block(g360)
    c: Block(g361)
    c: Block(g362)
    c: Block(g363)
    c: Block(g364)
    c: Block(g365)
    c: Block(g366)
    c: Block(g367)
    c: Block(g368)
    c: Block(g369)
    c: Block(g370)
    c: Block(g371)
    c: Block(g372)
    c: Block(g373)
    c: Block(g374)
    c: Block(g375)
    c: Block(g376)
    c: Block(g377)
    c: Block(g378)
    c: Block(g379)
    c: Block(g380)
    c: Block(g381)
    c: Block(g382)
    c: Block(g383)
    c: Block(g384)
    c: Block(g385)
    c: Block(g386)
    c: Block(g387)
    c: Block(g388)
    c: Block(g389)
    c: Block(g390)
    c: Block(g391)
    c: Block(g392)
    c: Block(g393)
    c: Block(g394)
    c: Block(g395)
    c: Block(g396)
    c: Block(g397)
    c: Block(g398)
    c: Block(g399)
    c: Block(g400)
    c: Block(g401)
    c: Block(g402)
    c: Block(g403)
    c: Block(g404)
    c: Block(g405)
    c: Block(g406)
    c: Block(g407)
    c: Block(g408)
    c: Block(g409)
    c: Block(g410)
    c: Block(g411)
    c: Block(g412)
    c: Block(g413)
    c: Block(g414)
    c: Block(g415)
    c: Block(g416)
    c: Block(g417)
    c: Block(g418)
    c: Block(g419)
    c: Block(g420)
    c: Block(g421)
    c: Block(g422)
    c: Block(g423)
    c: Block(g424)
    c: Block(g425)
    c: Block(g426)
    c: Block(g427)
    c: Block(g428)
    c: Block(g429)
    c: Block(g430)
    c: Block(g431)
    c: Block(g432)
    c: Block(g433)
    c: Block(g434)
    c: Block(g435)
    c: Block(g436)
    c: Block(g437)
    c: Block(g438)
    c: Block(g439)
    c: Block(g440)
    c: Block(g441)
    c: Block(g442)
    c: Block(g443)
    c: Block(g444)
    c: Block(g445)
    c: Block(g446)
    c: Block(g447)
    c: Block(g448)
    c: Block(g449)
    c: Block(g450)
    c: Block(g451)
    c: Block(g452)
    c: Block(g453)
    c: Block(g454)
    c: Block(g455)
    c: Block(g456)
    c: Block(g457)
    c: Block(g458)
    c: Block(g459)
    c: Block(g460)
    c: Block(g461)
    c: Block(g462)
    c: Block(g463)
    c: Block(g464)
    c: Block(g465)
    c: Block(g466)
    c: Block(g467)
    c: Block(g468)
    c: Block(g469)
    c: Block(g470)
    c: Block(g471)
    c: Block(g472)
    c: Block(g473)
    c: Block(g474)
    c: Block(g475)
    c: Block(g476)
    c: Block(g477)
    c: Block(g478)
    c: Block(g479)
    c: Block(g480)
    c: Block(g481)
    c: Block(g482)
    c: Block(g483)
    c: Block(g484)
    c: Block(g485)
    c: Block(g486)
    c: Block(g487)
    c: Block(g488)
    c: Block(g489)
    c: Block(g490)
    c: Block(g491)
    c: Block(g492)
    c: Block(g493)
    c: Block(g494)
    c: Block(g495)
    c: Block(g496)
    c: Block(g497)
    c: Block(g498)
    c: Block(g499)
    c: Block(g500)
    c: Block(g501)
    c: Block(g502)
    c: Block(g503)
    c: Block(g504)
    c: Block(g505)
    c: Block(g506)
    c: Block(g507)
    c: Block(g508)
    c: Block(g509)
    c: Block(g510)
    c: Block(g511)
    c: Block(g512)
    c: Block(g513)
    c: Block(g514)
    c: Block(g515)
    c: Block(g516)
    c: Block(g517)
    c: Block(g518)
    c: Block(g519)
    c: Block(g520)
    c: Block(g521)
    c: Block(g522)
    c: Block(g523)
    c: Block(g524)
    c: Block(g525)
    c: Block(g526)
    c: Block(g527)
    c: Block(g528)
    c: Block(g529)
    c: Block(g530)
    c: Block(g531)
    c: Block(g532)
    c: Block(g533)
    c: Block(g534)
    c: Block(g535)
    c: Block(g536)
    c: Block(g537)
    c: Block(g538)
    c: Block(g539)
    c: Block(g540)
    c: Block(g541)
    c: Block(g542)
    c: Block(g543)
    c: Block(g544)
    c: Block(g545)
    c: Block(g546)
    c: Block(g547)
    c: Block(g548)
    c: Block(g549)
    c: Block(g550)
    c: Block(g551)
    c: Block(g552)
    c: Block(g553)
    c: Block(g554)
    c: Block(g555)
    c: Block(g556)
    c: Block(g557)
    c: Block(g558)
    c: Block(g559)
    c: Block(g560)
    c: Block(g561)
    c: Block(g562)
    c: Block(g563)
    c: Block(g564)
    c: Block(g565)
    c: Block(g566)
    c: Block(g567)
    c: Block(g568)
    c: Block(g569)
    c: Block(g570)
    c: Block(g571)
    c: Block(g572)
    c: Block(g573)
    c: Block(g574)
    c: Block(g575)
    c: Block(g576)
    c: Block(g577)
    c: Block(g578)
    c: Block(g579)
    c: Block(g580)
    c: Block(g581)
    c: Block(g582)
    c: Block(g583)
    c: Block(g584)
    c: Block(g585)
    c: Block(g586)
    c: Block(g587)
    c: Block(g588)
    c: Block(g589)
    c: Block(g590)
    c: Block(g591)
    c: Block(g592)
    c: Block(g593)
    c: Block(g594)
    c: Block(g595)
    c: Block(g596)
    c: Block(g597)
    c: Block(g598)
    c: Block(g599)
    c: Block(g600)
    c: Block(g601)
    c: Block(g602)
    c: Block(g603)
    c: Block(g604)
    c: Block(g605)
    c: Block(g606)
    c: Block(g607)
    c: Block(g608)
    c: Block(g609)
    c: Block(g610)
    c: Block(g611)
    c: Block(g612)
    c: Block(g613)
    c: Block(g614)
    c: Block(g615)
    c: Block(g616)
    c: Block(g617)
    c: Block(g618)
    c: Block(g619)
    c: Block(g620)
    c: Block(g621)
    c: Block(g622)
    c: Block(g623)
    c: Block(g624)
    c: Block(g625)
    c: Block(g626)
    c: Block(g627)
    c: Block(g628)
    c: Block(g629)
    c: Block(g630)
    c: Block(g631)
    c: Block(g632)
    c: Block(g633)
    c: Block(g634)
    c: Block(g635)
    c: Block(g636)
    c: Block(g637)
    c: Block(g638)
    c: Block(g639)
    c: Block(g640)
    c: Block(g641)
    c: Block(g642)
    c: Block(g643)
    c: Block(g644)
    c: Block(g645)
    c: Block(g646)
    c: Block(g647)
    c: Block(g648)
    c: Block(g649)
    c: Block(g650)
    c: Block(g651)
    c: Block(g652)
    c: Block(g653)
    c: Block(g654)
    c: Block(g655)
    c: Block(g656)
    c: Block(g657)
    c: Block(g658)
    c: Block(g659)
    c: Block(g660)
    c: Block(g661)
    c: Block(g662)
    c: Block(g663)
    c: Block(g664)
    c: Block(g665)
    c: Block(g666)
    c: Block(g667)
    c: Block(g668)
    c: Block(g669)
    c: Block(g670)
    c: Block(g671)
    c: Block(g672)
    c: Block(g673)
    c: Block(g674)
    c: Block(g675)
    c: Block(g676)
    c: Block(g677)
    c: Block(g678)
    c: Block(g679)
    c: Block(g680)
    c: Block(g681)
    c: Block(g682)
    c: Block(g683)
    c: Block(g684)
    c: Block(g685)
    c: Block(g686)
    c: Block(g687)
    c: Block(g688)
    c: Block(g689)
    c: Block(g690)
    c: Block(g691)
    c: Block(g692)
    c: Block(g693)
    c: Block(g694)
    c: Block(g695)
    c: Block(g696)
    c: Block(g697)
    c: Block(g698)
    c: Block(g699)
    c: Block(g700)
    c: Block(g701)
    c: Block(g702)
    c: Block(g703)
    c: Block(g704)
    c: Block(g705)
    c: Block(g706)
    c: Block(g707)
    c: Block(g708)
    c: Block(g709)
    c: Block(g710)
    c: Block(g711)
    c: Block(g712)
    c: Block(g713)
    c: Block(g714)
    c: Block(g715)
    c: Block(g716)
    c: Block(g717)
    c: Block(g718)
    c: Block(g719)
    c: Block(g720)
    c: Block(g721)
    c: Block(g722)
    c: Block(g723)
    c: Block(g724)
    c: Block(g725)
    c: Block(g726)
    c: Block(g727)
    c: Block(g728)
    c: Block(g729)
    c: Block(g730)
    c: Block(g731)
    c: Block(g732)
    c: Block(g733)
    c: Block(g734)
    c: Block(g735)
    c: Block(g736)
    c: Block(g737)
    c: Block(g738)
    c: Block(g739)
    c: Block(g740)
    c: Block(g741)
    c: Block(g742)
    c: Block(g743)
    c: Block(g744)
    c: Block(g745)
    c: Block(g746)
    c: Block(g747)
    c: Block(g748)
    c: Block(g749)
    c: Block(g750)
    c: Block(g751)
    c: Block(g752)
    c: Block(g753)
    c: Block(g754)
    c: Block(g755)
    c: Block(g756)
    c: Block(g757)
    c: Block(g758)
    c: Block(g759)
    c: Block(g760)
    c: Block(g761)
    c: Block(g762)
    c: Block(g763)
    c: Block(g764)
    c: Block(g765)
    c: Block(g766)
    c: Block(g767)
    c: Block(g768)
    c: Block(g769)
    c: Block(g770)
    c: Block(g771)
    c: Block(g772)
    c: Block(g773)
    c: Block(g774)
    c: Block(g775)
    c: Block(g776)
    c: Block(g777)
    c: Block(g778)
    c: Block(g779)
    c: Block(g780)
    c: Block(g781)
    c: Block(g782)
    c: Block(g783)
    c: Block(g784)
    c: Block(g785)
    c: Block(g786)
    c: Block(g787)
    c: Block(g788)
    c: Block(g789)
    c: Block(g790)
    c: Block(g791)
    c: Block(g792)
    c: Block(g793)
    c: Block(g794)
    c: Block(g795)
    c: Block(g796)
    c: Block(g797)
    c: Block(g798)
    c: Block(g799)
    c: Block(g800)
    c: Block(g801)
    c: Block(g802)
    c: Block(g803)
    c: Block(g804)
    c: Block(g805)
    c: Block(g806)
    c: Block(g807)
    c: Block(g808)
    c: Block(g809)
    c: Block(g810)
    c: Block(g811)
    c: Block(g812)
    c: Block(g813)
    c: Block(g814)
    c: Block(g815)
    c: Block(g816)
    c: Block(g817)
    c: Block(g818)
    c: Block(g819)
    c: Block(g820)
    c: Block(g821)
    c: Block(g822)
    c: Block(g823)
    c: Block(g824)
    c: Block(g825)
    c: Block(g826)
    c: Block(g827)
    c: Block(g828)
    c: Block(g829)
    c: Block(g830)
    c: Block(g831)
    c: Block(g832)
    c: Block(g833)
    c: Block(g834)
    c: Block(g835)
    c: Block(g836)
    c: Block(g837)
    c: Block(g838)
    c: Block(g839)
    c: Block(g840)
    c: Block(g841)
    c: Block(g842)
    c: Block(g843)
    c: Block(g844)
    c: Block(g845)
    c: Block(g846)
    c: Block(g847)
    c: Block(g848)
    c: Block(g849)
    c: Block(g850)
    c: Block(g851)
    c: Block(g852)
    c: Block(g853)
    c: Block(g854)
    c: Block(g855)
    c: Block(g856)
    c: Block(g857)
    c: Block(g858)
    c: Block(g859)
    c: Block(g860)
    c: Block(g861)
    c: Block(g862)
    c: Block(g863)
    c: Block(g864)
    c: Block(g865)
    c: Block(g866)
    c: Block(g867)
    c: Block(g868)
    c: Block(g869)
    c: Block(g870)
    c: Block(g871)
    c: Block(g872)
    c: Block(g873)
    c: Block(g874)
    c: Block(g875)
    c: Block(g876)
    c: Block(g877)
    c: Block(g878)
    c: Block(g879)
    c: Block(g880)
    c: Block(g881)
    c: Block(g882)
    c: Block(g883)
    c: Block(g884)
    c: Block(g885)
    c: Block(g886)
    c: Block(g887)
    c: Block(g888)
    c: Block(g889)
    c: Block(g890)
    c: Block(g891)
    c: Block(g892)
    c: Block(g893)
    c: Block(g894)
    c: Block(g895)
    c: Block(g896)
    c: Block(g897)
    c: Block(g898)
    c: Block(g899)
    c: Block(g900)
    c: Block(g901)
    c: Block(g902)
    c: Block(g903)
    c: Block(g904)
    c: Block(g905)
    c: Block(g906)
    c: Block(g907)
    c: Block(g908)
    c: Block(g909)
    c: Block(g910)
    c: Block(g911)
    c: Block(g912)
    c: Block(g913)
    c: Block(g914)
    c: Block(g915)
    c: Block(g916)
    c: Block(g917)
    c: Block(g918)
    c: Block(g919)
    c: Block(g920)
    c: Block(g921)
    c: Block(g922)
    c: Block(g923)
    c: Block(g924)
    c: Block(g925)
    c: Vertical(g926)
    c: Coincident(g927,g926)
    c: Horizontal(g927)
    c: Coincident(g928,g927)
    c: Vertical(g928)
    c: Coincident(g929,g928)
    c: Coincident(g929,g926)
    c: Horizontal(g929)
    c: DistanceY(g928,g928) = 140.9
    c: DistanceX(g927,g927) = 407.7
    c: DistanceY(g921,g926) = 6.09
    c: DistanceX(g921,g926) = 5.09
    c: Coincident(g930,g931)
    c: Coincident(g931,g932)
    c: Coincident(g932,g933)
    c: Coincident(g933,g930)
    c: Horizontal(g930)
    c: Horizontal(g932)
    c: Vertical(g931)
    c: Vertical(g933)
    c: Parallel(g933,g234)
    c: Vertical(g234,g932)
    c: DistanceY(g96,g930) = 2.5
    c: Vertical(g931,g267)
    c: DistanceY(g232,g932) = 5
